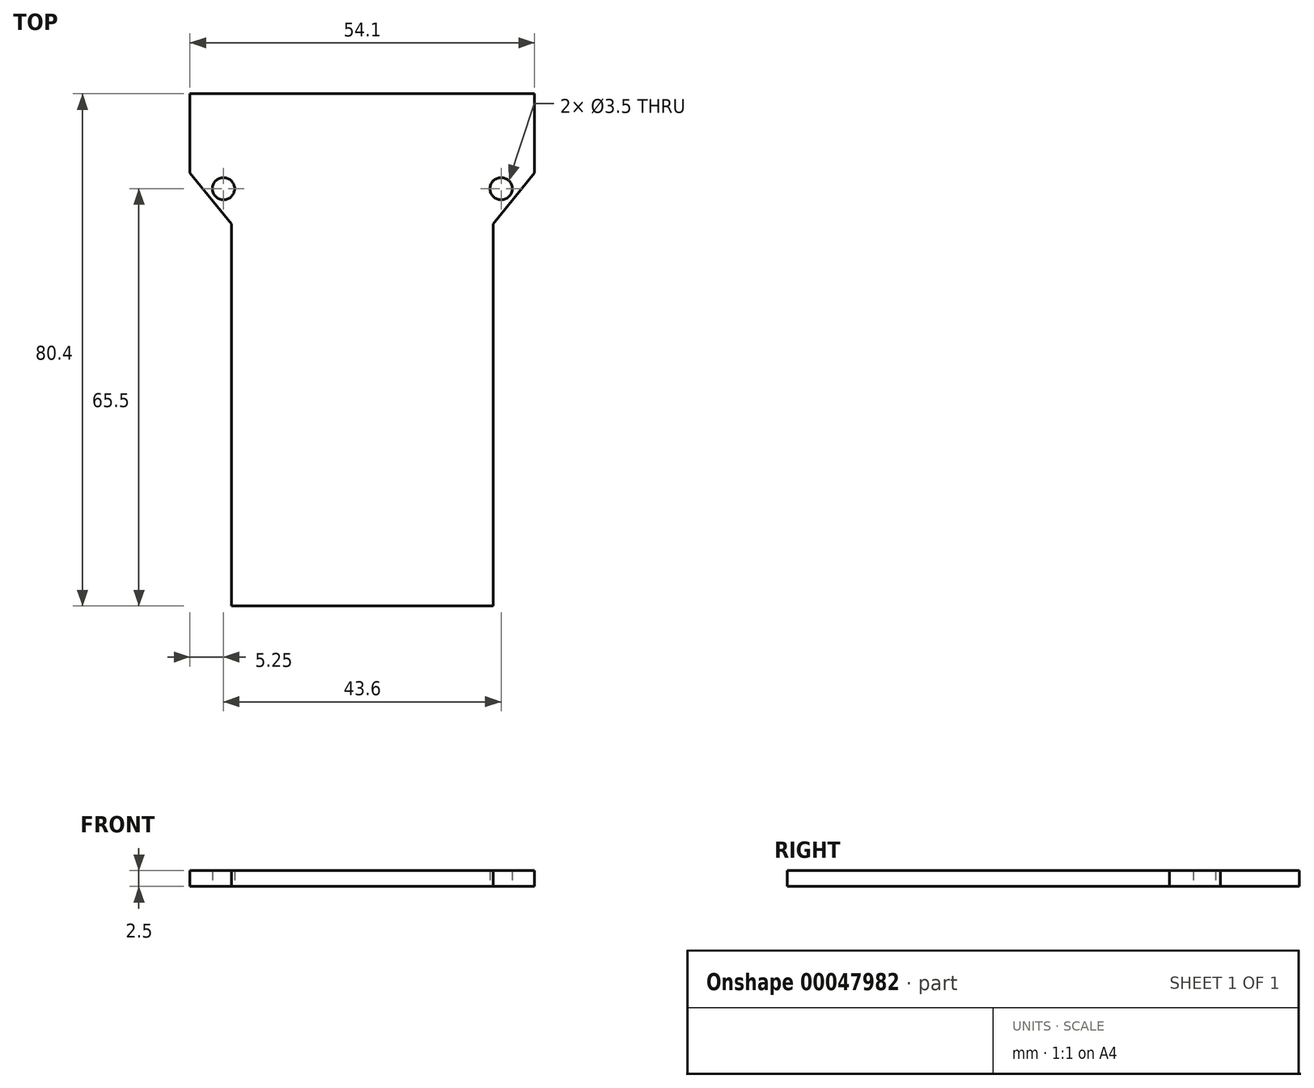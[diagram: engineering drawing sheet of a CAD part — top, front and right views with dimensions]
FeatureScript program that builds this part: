
annotation { "Feature Type Name" : "Feature", "Feature Type Description" : "" }
export const myFeature = defineFeature(function(context is Context, id is Id, definition is map)
    precondition{}
    {
        {
            var Q0;
            Q0=qCreatedBy(makeId("Top.planeOp"),FACE);
            var sketch = newSketch(context, id + "F0", { "sketchPlane" : qUnion([Q0])});
            skLineSegment(sketch, "E0", {"start": v(-20.55, 0) * mm, "end": v(-20.55, -60) * mm});
            skLineSegment(sketch, "E1", {"start": v(-20.55, -60) * mm, "end": v(0, -60) * mm});
            skLineSegment(sketch, "E2", {"start": v(0, -60) * mm, "end": v(20.55, -60) * mm});
            skLineSegment(sketch, "E3", {"start": v(20.55, -60) * mm, "end": v(20.55, 0) * mm});
            skLineSegment(sketch, "E4", {"start": v(0, 20.4) * mm, "end": v(-27.05, 20.4) * mm});
            skLineSegment(sketch, "E5", {"start": v(-27.05, 20.4) * mm, "end": v(0, 20.4) * mm});
            skLineSegment(sketch, "E6", {"start": v(0, 20.4) * mm, "end": v(27.05, 20.4) * mm});
            skLineSegment(sketch, "E7", {"start": v(-27.05, 20.4) * mm, "end": v(-27.05, 8) * mm});
            skLineSegment(sketch, "E8", {"start": v(-27.05, 8) * mm, "end": v(-20.55, 0) * mm});
            skLineSegment(sketch, "E9", {"start": v(27.05, 20.4) * mm, "end": v(27.05, 8) * mm});
            skLineSegment(sketch, "E10", {"start": v(27.05, 8) * mm, "end": v(20.55, 0) * mm});
            skLineSegment(sketch, "E11", {"start": v(0, 20.4) * mm, "end": v(0, 0) * mm, "construction": true});
            skLineSegment(sketch, "E12", {"start": v(0, 0) * mm, "end": v(0, -60) * mm, "construction": true});
            skCircle(sketch, "E13", {"center": v(-21.8, 5.5) * mm, "radius": 1.75 * mm});
            skLineSegment(sketch, "E14", {"start": v(-27.05, 8) * mm, "end": v(27.05, 8) * mm, "construction": true});
            skCircle(sketch, "E15.MirrorC", {"center": v(21.8, 5.5) * mm, "radius": 1.75 * mm});
            skSolve(sketch);
        }
        {
            var Q0;
            Q0 = qSketchRegion(id + "F0", true);
            extrude(context, id + "F1", {"entities" : qUnion([Q0]), "depth" : 2.5 * mm});
        }
    });
